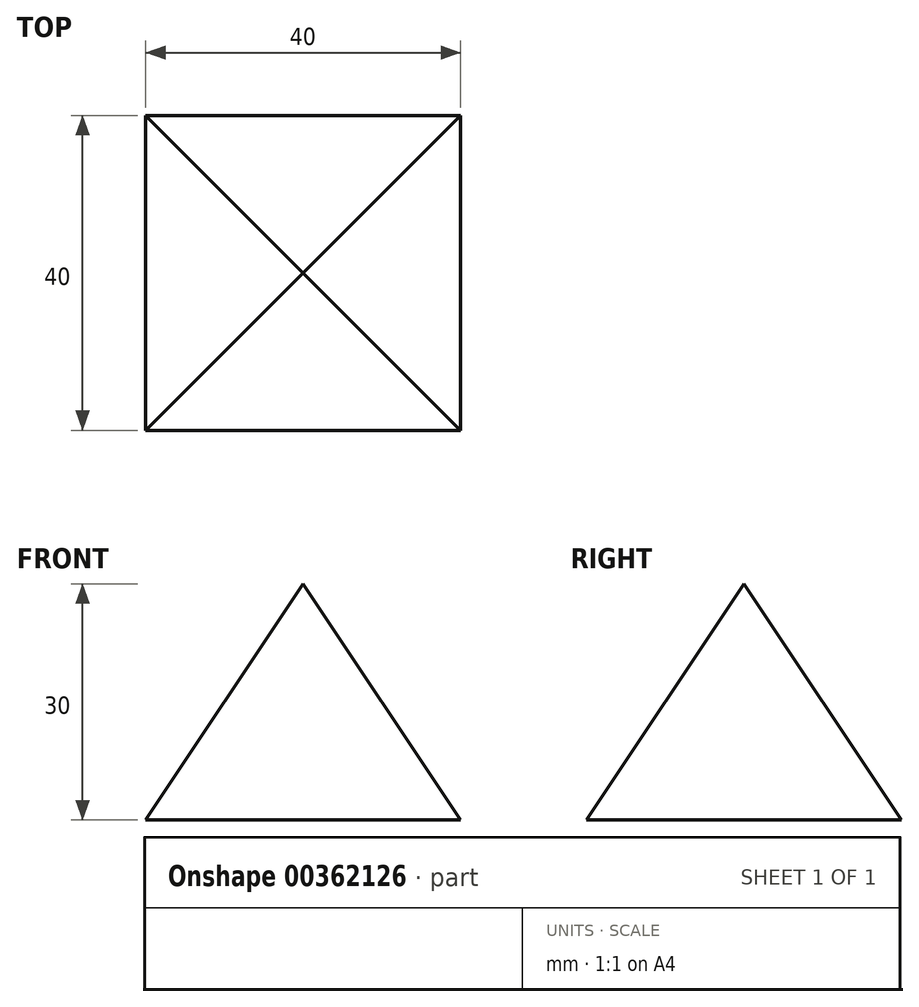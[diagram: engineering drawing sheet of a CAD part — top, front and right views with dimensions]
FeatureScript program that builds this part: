
annotation { "Feature Type Name" : "Feature", "Feature Type Description" : "" }
export const myFeature = defineFeature(function(context is Context, id is Id, definition is map)
    precondition{}
    {
        {
            var Q0;
            Q0=qCreatedBy(makeId("Top.planeOp"),FACE);
            var sketch = newSketch(context, id + "F0", { "sketchPlane" : qUnion([Q0])});
            skLineSegment(sketch, "E0.bottom", {"start": v(-20, 20) * mm, "end": v(20, 20) * mm});
            skLineSegment(sketch, "E0.top", {"start": v(-20, -20) * mm, "end": v(20, -20) * mm});
            skLineSegment(sketch, "E0.left", {"start": v(-20, 20) * mm, "end": v(-20, -20) * mm});
            skLineSegment(sketch, "E0.right", {"start": v(20, 20) * mm, "end": v(20, -20) * mm});
            skPoint(sketch, "E0.middle", {"position": v(0, 0) * mm});
            skSolve(sketch);
        }
        {
            var Q0;
            Q0=makeQuery(id+"F0.imprint","IMPRINT",FACE,{"disambiguationData":[TD([[makeQuery(id+"F0.imprint","IMPRINT",EDGE,{"derivedFrom":sQuery(id+"F0.wireOp",EDGE,"E0.bottom")}),-1.0]])]});
            extrude(context, id + "F1", {"entities" : qUnion([Q0]), "depth" : 30 * mm, "offsetDistance" : 25 * mm});
        }
        {
            var Q0;
            Q0=makeQuery(id+"F1.opExtrude","CAP_EDGE",EDGE,{"disambiguationData":[OSD([sQuery(id+"F0.wireOp",EDGE,"E0.left")])],"isStart":false});
            var Q1;
            Q1=makeQuery(id+"F1.opExtrude","CAP_EDGE",EDGE,{"disambiguationData":[OSD([sQuery(id+"F0.wireOp",EDGE,"E0.bottom")])],"isStart":false});
            var Q2;
            Q2=makeQuery(id+"F1.opExtrude","CAP_EDGE",EDGE,{"disambiguationData":[OSD([sQuery(id+"F0.wireOp",EDGE,"E0.top")])],"isStart":false});
            var Q3;
            Q3=makeQuery(id+"F1.opExtrude","CAP_EDGE",EDGE,{"disambiguationData":[OSD([sQuery(id+"F0.wireOp",EDGE,"E0.right")])],"isStart":false});
            chamfer(context, id + "F2", {"entities" : qUnion([Q0, Q1, Q2, Q3]), "chamferType" : ChamferType.TWO_OFFSETS, "width1" : 20 * mm, "oppositeDirection" : false, "width2" : 30 * mm, "tangentPropagation" : true});
        }
    });
